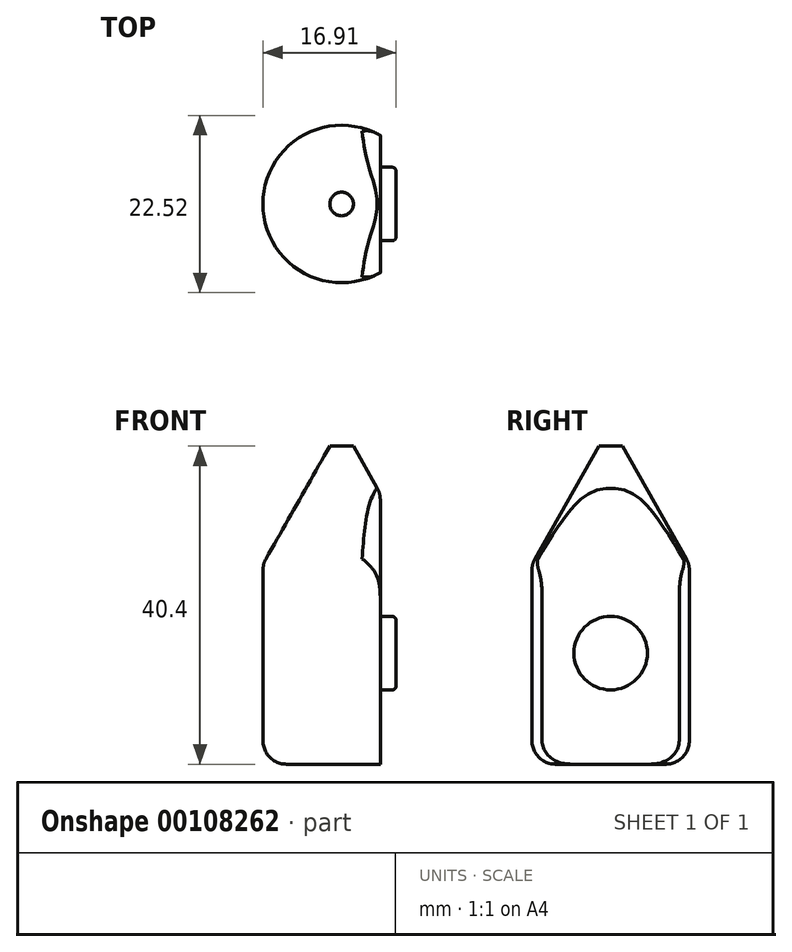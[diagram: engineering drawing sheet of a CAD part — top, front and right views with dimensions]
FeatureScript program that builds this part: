
annotation { "Feature Type Name" : "Feature", "Feature Type Description" : "" }
export const myFeature = defineFeature(function(context is Context, id is Id, definition is map)
    precondition{}
    {
        {
            var Q0;
            Q0=qCreatedBy(makeId("Right.planeOp"),FACE);
            var sketch = newSketch(context, id + "F0", { "sketchPlane" : qUnion([Q0])});
            skLineSegment(sketch, "E0", {"start": v(0, 15) * mm, "end": v(1.5, 15) * mm});
            skLineSegment(sketch, "E1", {"start": v(1.5, 15) * mm, "end": v(10, 0) * mm});
            skLineSegment(sketch, "E2", {"start": v(10, 0) * mm, "end": v(0, 0) * mm});
            skLineSegment(sketch, "E3", {"start": v(0, 0) * mm, "end": v(0, 15) * mm});
            skSolve(sketch);
        }
        {
            var Q0;
            Q0=makeQuery(id+"F0.imprint","IMPRINT",FACE,{"disambiguationData":[TD([[makeQuery(id+"F0.imprint","IMPRINT",EDGE,{"derivedFrom":sQuery(id+"F0.wireOp",EDGE,"E0")}),-1.0]])]});
            var Q1;
            Q1=sQuery(id+"F0.wireOp",EDGE,"E3");
            revolve(context, id + "F1", {"entities" : qUnion([Q0]), "axis" : qUnion([Q1]), "revolveType" : RevolveType.FULL});
        }
        {
            var Q0;
            Q0=makeQuery(id+"F1.opRevolve","SWEPT_FACE",FACE,{"disambiguationData":[OSD([sQuery(id+"F0.wireOp",EDGE,"E2")])]});
            extrude(context, id + "F2", {"entities" : qUnion([Q0]), "operationType" : NewBodyOperationType.ADD, "depth" : 25.4 * mm});
        }
        {
            var Q0;
            Q0=makeQuery(id+"F2.opExtrude","CAP_FACE",FACE,{"disambiguationData":[OSD([sQuery(id+"F0.wireOp",EDGE,"E2")])],"isStart":false});
            var sketch = newSketch(context, id + "F3", { "sketchPlane" : qUnion([Q0])});
            skLineSegment(sketch, "E4", {"start": v(4.9, 8.71) * mm, "end": v(4.9, -8.71) * mm});
            skSolve(sketch);
        }
        {
            var Q0;
            Q0 = qSketchRegion(id + "F3", true);
            var Q1;
            {var subQ0=sQuery(id+"F3.wireOp",EDGE,"E4");Q1=makeQuery(id+"F3.imprint","IMPRINT",FACE,{"disambiguationData":[TD([[makeQuery(id+"F3.imprint","IMPRINT",EDGE,{"derivedFrom":subQ0}),1.0]])]});}
            extrude(context, id + "F4", {"entities" : qUnion([Q0, Q1]), "operationType" : NewBodyOperationType.REMOVE, "oppositeDirection" : true, "depth" : 50.8 * mm});
        }
        {
            var Q0;
            Q0=makeQuery(id+"F4.boolean.opBoolean","COPY",EDGE,{"derivedFrom":makeQuery(id+"F4.opExtrude","CAP_EDGE",EDGE,{"disambiguationData":[OSD([sQuery(id+"F3.wireOp",EDGE,"E4")])],"isStart":true})});
            var Q1;
            Q1=makeQuery(id+"F4.boolean.opBoolean","INTERSECT",EDGE,{"derivedFrom":[makeQuery(id+"F1.opRevolve","SWEPT_FACE",FACE,{"disambiguationData":[OSD([sQuery(id+"F0.wireOp",EDGE,"E1")])]}),makeQuery(id+"F4.opExtrude","SWEPT_FACE",FACE,{"disambiguationData":[OSD([sQuery(id+"F3.wireOp",EDGE,"E4")])]})]});
            var Q2;
            {var subQ0=sQuery(id+"F3.wireOp",EDGE,"E4");var subQ1=sQuery(id+"F0.wireOp",EDGE,"E2");var subQ2=sQuery(id+"F0.wireOp",EDGE,"E1");Q2=makeQuery(id+"F4.boolean.opBoolean","COPY",EDGE,{"derivedFrom":makeQuery(id+"F4.opExtrude","SWEPT_EDGE",EDGE,{"disambiguationData":[OSD([subQ2,subQ1,subQ0]),TDD([makeQuery(id+"F3.imprint","INTERSECT",VERTEX,{"disambiguationData":[OD(0.0)],"derivedFrom":[makeQuery(id+"F2.opExtrude","CAP_EDGE",EDGE,{"disambiguationData":[OSD([subQ2,subQ1])],"isStart":false}),subQ0]})])]})});}
            var Q3;
            {var subQ0=sQuery(id+"F3.wireOp",EDGE,"E4");var subQ1=sQuery(id+"F0.wireOp",EDGE,"E2");var subQ2=sQuery(id+"F0.wireOp",EDGE,"E1");Q3=makeQuery(id+"F4.boolean.opBoolean","COPY",EDGE,{"derivedFrom":makeQuery(id+"F4.opExtrude","SWEPT_EDGE",EDGE,{"disambiguationData":[OSD([subQ2,subQ1,subQ0]),TDD([makeQuery(id+"F3.imprint","INTERSECT",VERTEX,{"disambiguationData":[OD(1.0)],"derivedFrom":[makeQuery(id+"F2.opExtrude","CAP_EDGE",EDGE,{"disambiguationData":[OSD([subQ2,subQ1])],"isStart":false}),subQ0]})])]})});}
            var Q4;
            Q4=makeQuery(id+"F2.opExtrude","CAP_EDGE",EDGE,{"disambiguationData":[OSD([sQuery(id+"F0.wireOp",EDGE,"E1"),sQuery(id+"F0.wireOp",EDGE,"E2")])],"isStart":false});
            var Q5;
            {var subQ0=sQuery(id+"F0.wireOp",EDGE,"E2");var subQ1=sQuery(id+"F0.wireOp",EDGE,"E1");Q5=makeQuery(id+"F2.boolean.opBoolean","MERGE",EDGE,{"derivedFrom":[makeQuery(id+"F1.opRevolve","SWEPT_EDGE",EDGE,{"disambiguationData":[OSD([subQ1,subQ0])]}),makeQuery(id+"F2.opExtrude","CAP_EDGE",EDGE,{"disambiguationData":[OSD([subQ1,subQ0])],"isStart":true})]});}
            fillet(context, id + "F5", {"entities" : qUnion([Q0, Q1, Q2, Q3, Q4, Q5]), "radius" : 3 * mm, "tangentPropagation" : true, "allowEdgeOverflow" : false});
        }
        {
            var Q0;
            Q0=makeQuery(id+"F4.boolean.opBoolean","COPY",FACE,{"derivedFrom":makeQuery(id+"F4.opExtrude","SWEPT_FACE",FACE,{"disambiguationData":[OSD([sQuery(id+"F3.wireOp",EDGE,"E4")])]})});
            var sketch = newSketch(context, id + "F6", { "sketchPlane" : qUnion([Q0])});
            skCircle(sketch, "E5", {"center": v(0, -11.3) * mm, "radius": 4.67 * mm});
            skSolve(sketch);
        }
        {
            var Q0;
            Q0=makeQuery(id+"F6.imprint","IMPRINT",FACE,{"disambiguationData":[TD([[makeQuery(id+"F6.imprint","IMPRINT",EDGE,{"derivedFrom":sQuery(id+"F6.wireOp",EDGE,"E5")}),1.0]])]});
            extrude(context, id + "F7", {"entities" : qUnion([Q0]), "operationType" : NewBodyOperationType.ADD, "depth" : 2 * mm});
        }
        {
            var Q0;
            Q0=makeQuery(id+"F7.opExtrude","CAP_EDGE",EDGE,{"disambiguationData":[OSD([sQuery(id+"F6.wireOp",EDGE,"E5")])],"isStart":false});
            fillet(context, id + "F8", {"entities" : qUnion([Q0]), "radius" : 0.5 * mm, "tangentPropagation" : true, "allowEdgeOverflow" : false});
        }
    });
